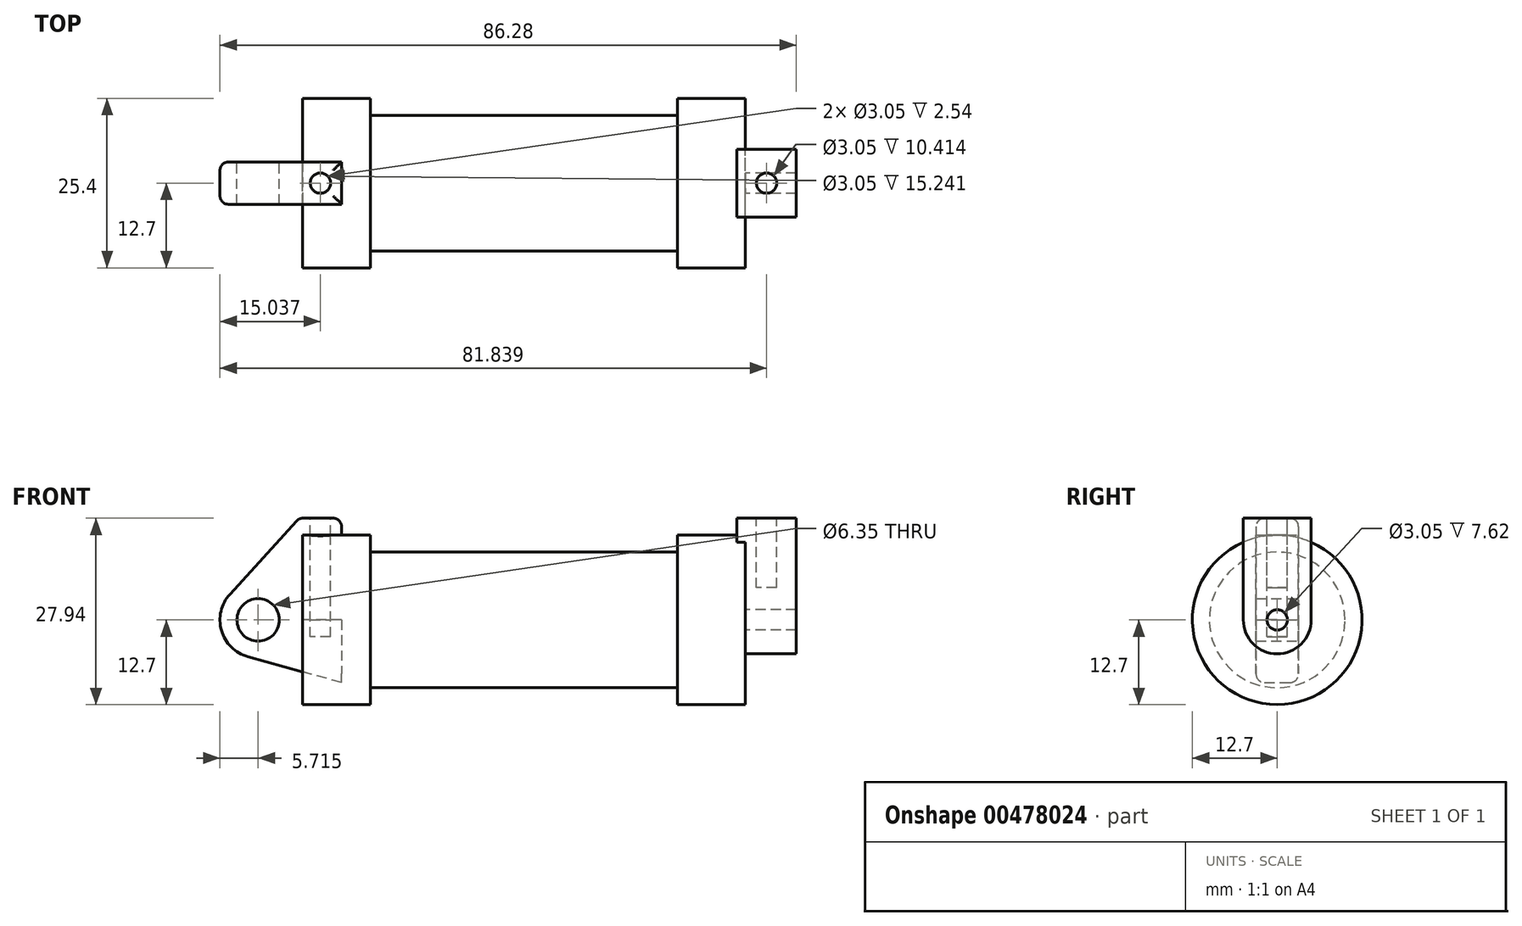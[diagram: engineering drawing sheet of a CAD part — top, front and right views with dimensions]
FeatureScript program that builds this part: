
annotation { "Feature Type Name" : "Feature", "Feature Type Description" : "" }
export const myFeature = defineFeature(function(context is Context, id is Id, definition is map)
    precondition{}
    {
        {
            var Q0;
            Q0=qCreatedBy(makeId("Front.planeOp"),FACE);
            var sketch = newSketch(context, id + "F0", { "sketchPlane" : qUnion([Q0])});
            skLineSegment(sketch, "E0", {"start": v(0, 0) * mm, "end": v(0, 12.7) * mm});
            skLineSegment(sketch, "E1", {"start": v(0, 12.7) * mm, "end": v(10.16, 12.7) * mm});
            skLineSegment(sketch, "E2", {"start": v(10.16, 12.7) * mm, "end": v(10.16, 10.16) * mm});
            skLineSegment(sketch, "E3", {"start": v(10.16, 10.16) * mm, "end": v(56.13, 10.16) * mm});
            skLineSegment(sketch, "E4", {"start": v(56.13, 10.16) * mm, "end": v(56.13, 12.7) * mm});
            skLineSegment(sketch, "E5", {"start": v(56.13, 12.7) * mm, "end": v(66.3, 12.7) * mm});
            skLineSegment(sketch, "E6", {"start": v(66.3, 12.7) * mm, "end": v(66.3, 0) * mm});
            skLineSegment(sketch, "E7", {"start": v(66.3, 0) * mm, "end": v(0, 0) * mm});
            skLineSegment(sketch, "E8", {"start": v(5.84, 15.24) * mm, "end": v(-0.5, 15.24) * mm});
            skLineSegment(sketch, "E9", {"start": v(-0.5, 15.24) * mm, "end": v(-10.88, 3.85) * mm});
            skLineSegment(sketch, "E10", {"start": v(0, 0) * mm, "end": v(-6.65, 0) * mm});
            skCircle(sketch, "E11", {"center": v(-6.65, 0) * mm, "radius": 5.72 * mm});
            skCircle(sketch, "E12", {"center": v(-6.65, 0) * mm, "radius": 3.18 * mm});
            skLineSegment(sketch, "E13", {"start": v(5.84, 15.24) * mm, "end": v(5.84, -9.4) * mm});
            skLineSegment(sketch, "E14", {"start": v(5.84, -9.4) * mm, "end": v(-8.18, -5.5) * mm});
            skSolve(sketch);
        }
        {
            var Q0;
            {var subQ0=sQuery(id+"F0.wireOp",EDGE,"E2");Q0=makeQuery(id+"F0.imprint","IMPRINT",FACE,{"disambiguationData":[TD([[makeQuery(id+"F0.imprint","IMPRINT",EDGE,{"derivedFrom":subQ0}),-1.0]])]});}
            var Q1;
            {var subQ0=sQuery(id+"F0.wireOp",EDGE,"E0");Q1=makeQuery(id+"F0.imprint","IMPRINT",FACE,{"disambiguationData":[TD([[makeQuery(id+"F0.imprint","IMPRINT",EDGE,{"derivedFrom":subQ0}),-1.0]])]});}
            var Q2;
            Q2=sQuery(id+"F0.wireOp",EDGE,"E7");
            revolve(context, id + "F1", {"entities" : qUnion([Q0, Q1]), "axis" : qUnion([Q2]), "revolveType" : RevolveType.FULL});
        }
        {
            var Q0;
            {var subQ5=sQuery(id+"F0.wireOp",EDGE,"E12");Q0=makeQuery(id+"F0.imprint","IMPRINT",FACE,{"disambiguationData":[TD([[makeQuery(id+"F0.imprint","IMPRINT",EDGE,{"derivedFrom":subQ5}),-1.0]])]});}
            var Q1;
            {var subQ0=sQuery(id+"F0.wireOp",EDGE,"E14");Q1=makeQuery(id+"F0.imprint","IMPRINT",FACE,{"disambiguationData":[TD([[makeQuery(id+"F0.imprint","IMPRINT",EDGE,{"derivedFrom":subQ0}),-1.0]])]});}
            var Q2;
            {var subQ1=sQuery(id+"F0.wireOp",EDGE,"E0");Q2=makeQuery(id+"F0.imprint","IMPRINT",FACE,{"disambiguationData":[TD([[makeQuery(id+"F0.imprint","IMPRINT",EDGE,{"derivedFrom":subQ1}),1.0]])]});}
            var Q3;
            Q3 = qSketchRegion(id + "F3", true);
            extrude(context, id + "F2", {"entities" : qUnion([Q0, Q1, Q2, Q3]), "endBound" : BoundingType.SYMMETRIC, "depth" : 6.35 * mm});
        }
        {
            var Q0;
            Q0=makeQuery(id+"F1.opRevolve","SWEPT_FACE",FACE,{"disambiguationData":[OSD([sQuery(id+"F0.wireOp",EDGE,"E6")])]});
            var sketch = newSketch(context, id + "F3", { "sketchPlane" : qUnion([Q0])});
            skCircle(sketch, "E15", {"center": v(0, 0) * mm, "radius": 1.52 * mm});
            skCircle(sketch, "E16", {"center": v(0, 0) * mm, "radius": 5.08 * mm});
            skLineSegment(sketch, "E17", {"start": v(-5.08, 0) * mm, "end": v(-5.08, 15.24) * mm});
            skLineSegment(sketch, "E18", {"start": v(5.08, 0) * mm, "end": v(5.08, 15.24) * mm});
            skLineSegment(sketch, "E19", {"start": v(-5.08, 15.24) * mm, "end": v(5.08, 15.24) * mm});
            skSolve(sketch);
        }
        {
            var Q0;
            {var subQ0=sQuery(id+"F3.wireOp",EDGE,"E19");Q0=makeQuery(id+"F3.imprint","IMPRINT",FACE,{"disambiguationData":[TD([[makeQuery(id+"F3.imprint","IMPRINT",EDGE,{"derivedFrom":subQ0}),-1.0]])]});}
            var Q1;
            {var subQ0=sQuery(id+"F3.wireOp",EDGE,"E17");var subQ1=sQuery(id+"F3.wireOp",EDGE,"E16");var subQ2=makeQuery(id+"F3.imprint","INTERSECT",VERTEX,{"derivedFrom":[subQ1,subQ0]});Q1=makeQuery(id+"F3.imprint","IMPRINT",FACE,{"disambiguationData":[TD([[makeQuery(id+"F3.imprint","IMPRINT",EDGE,{"disambiguationData":[TD([[subQ2,1.0]])],"derivedFrom":subQ1}),-1.0]])]});}
            var Q2;
            Q2=makeQuery(id+"F3.imprint","IMPRINT",FACE,{"disambiguationData":[TD([[makeQuery(id+"F3.imprint","IMPRINT",EDGE,{"derivedFrom":sQuery(id+"F3.wireOp",EDGE,"E15")}),-1.0]])]});
            extrude(context, id + "F4", {"entities" : qUnion([Q0, Q1, Q2]), "operationType" : NewBodyOperationType.ADD, "depth" : 7.62 * mm});
        }
        {
            var Q0;
            Q0=makeQuery(id+"F4.opExtrude","CAP_FACE",FACE,{"disambiguationData":[OSD([sQuery(id+"F3.wireOp",EDGE,"E15"),sQuery(id+"F3.wireOp",EDGE,"E16"),sQuery(id+"F3.wireOp",EDGE,"E17"),sQuery(id+"F3.wireOp",EDGE,"E18"),sQuery(id+"F3.wireOp",EDGE,"E19")])],"isStart":true});
            var Q1;
            Q1=makeQuery(id+"F4.boolean.opBoolean","SPLIT",FACE,{"disambiguationData":[TD([makeQuery(id+"F4.opExtrude","SWEPT_FACE",FACE,{"disambiguationData":[OSD([sQuery(id+"F3.wireOp",EDGE,"E15")])]})])],"derivedFrom":makeQuery(id+"F1.opRevolve","SWEPT_FACE",FACE,{"disambiguationData":[OSD([sQuery(id+"F0.wireOp",EDGE,"E6")])]})});
            extrude(context, id + "F5", {"entities" : qUnion([Q0, Q1]), "operationType" : NewBodyOperationType.ADD, "depth" : 1.27 * mm});
        }
        {
            var Q0;
            {var subQ0=sQuery(id+"F3.wireOp",EDGE,"E19");Q0=makeQuery(id+"F5.boolean.opBoolean","MERGE",FACE,{"derivedFrom":[makeQuery(id+"F4.opExtrude","SWEPT_FACE",FACE,{"disambiguationData":[OSD([subQ0])]}),makeQuery(id+"F5.opExtrude","SWEPT_FACE",FACE,{"disambiguationData":[OSD([subQ0])]})]});}
            var sketch = newSketch(context, id + "F6", { "sketchPlane" : qUnion([Q0])});
            skCircle(sketch, "E20", {"center": v(69.47, 0) * mm, "radius": 1.52 * mm});
            skLineSegment(sketch, "E21", {"start": v(69.47, 5.08) * mm, "end": v(69.47, -5.08) * mm, "construction": true});
            skSolve(sketch);
        }
        {
            var Q0;
            Q0=makeQuery(id+"F6.imprint","IMPRINT",FACE,{"disambiguationData":[TD([[makeQuery(id+"F6.imprint","IMPRINT",EDGE,{"derivedFrom":sQuery(id+"F6.wireOp",EDGE,"E20")}),1.0]])]});
            var Q1;
            Q1=sQuery(id+"F6.wireOp",EDGE,"E20");
            extrude(context, id + "F7", {"entities" : qUnion([Q0]), "operationType" : NewBodyOperationType.REMOVE, "surfaceEntities" : qUnion([Q1]), "oppositeDirection" : true, "depth" : 10.4 * mm});
        }
        {
            var Q0;
            Q0=makeQuery(id+"F2.opExtrude","SWEPT_FACE",FACE,{"disambiguationData":[OSD([sQuery(id+"F0.wireOp",EDGE,"E8")])]});
            var sketch = newSketch(context, id + "F8", { "sketchPlane" : qUnion([Q0])});
            skLineSegment(sketch, "E22", {"start": v(2.67, 3.18) * mm, "end": v(2.67, -3.18) * mm, "construction": true});
            skCircle(sketch, "E23", {"center": v(2.67, 0) * mm, "radius": 1.52 * mm});
            skSolve(sketch);
        }
        {
            var Q0;
            Q0=makeQuery(id+"F8.imprint","IMPRINT",FACE,{"disambiguationData":[TD([[makeQuery(id+"F8.imprint","IMPRINT",EDGE,{"derivedFrom":sQuery(id+"F8.wireOp",EDGE,"E23")}),1.0]])]});
            var Q1;
            Q1=sQuery(id+"F8.wireOp",EDGE,"E23");
            extrude(context, id + "F9", {"entities" : qUnion([Q0]), "operationType" : NewBodyOperationType.REMOVE, "surfaceEntities" : qUnion([Q1]), "oppositeDirection" : true, "depth" : 17.78 * mm});
        }
        {
            var Q0;
            {var subQ0=sQuery(id+"F3.wireOp",EDGE,"E17");var subQ1=sQuery(id+"F3.wireOp",EDGE,"E16");var subQ2=makeQuery(id+"F3.imprint","INTERSECT",VERTEX,{"derivedFrom":[subQ1,subQ0]});Q0=makeQuery(id+"F3.imprint","IMPRINT",FACE,{"disambiguationData":[TD([[makeQuery(id+"F3.imprint","IMPRINT",EDGE,{"disambiguationData":[TD([[subQ2,1.0]])],"derivedFrom":subQ1}),-1.0]])]});}
            extrude(context, id + "F10", {"entities" : qUnion([Q0]), "operationType" : NewBodyOperationType.ADD, "oppositeDirection" : true, "depth" : 1.27 * mm});
        }
        {
            var Q0;
            {var subQ0=sQuery(id+"F0.wireOp",EDGE,"E5");var subQ1=sQuery(id+"F0.wireOp",EDGE,"E6");Q0=makeQuery(id+"F4.boolean.opBoolean","SPLIT",EDGE,{"disambiguationData":[topologyDisambiguationEdgeConnected([makeQuery(id+"F1.opRevolve","SWEPT_FACE",FACE,{"disambiguationData":[OSD([subQ1])]})])],"derivedFrom":makeQuery(id+"F1.opRevolve","SWEPT_EDGE",EDGE,{"disambiguationData":[OSD([subQ0,subQ1])]})});}
            var Q1;
            {var subQ0=sQuery(id+"F3.wireOp",EDGE,"E17");Q1=makeQuery(id+"F4.boolean.opBoolean","SPLIT",EDGE,{"disambiguationData":[topologyDisambiguationEdgeConnected([makeQuery(id+"F1.opRevolve","SWEPT_FACE",FACE,{"disambiguationData":[OSD([sQuery(id+"F0.wireOp",EDGE,"E6")])]})])],"derivedFrom":makeQuery(id+"F4.opExtrude","CAP_EDGE",EDGE,{"disambiguationData":[OSD([subQ0])],"isStart":true})});}
            var Q2;
            Q2=makeQuery(id+"F4.opExtrude","CAP_EDGE",EDGE,{"disambiguationData":[OSD([sQuery(id+"F3.wireOp",EDGE,"E17")])],"isStart":false});
            var Q3;
            Q3=makeQuery(id+"F4.opExtrude","CAP_EDGE",EDGE,{"disambiguationData":[OSD([sQuery(id+"F3.wireOp",EDGE,"E19")])],"isStart":false});
            var Q4;
            {var subQ0=sQuery(id+"F3.wireOp",EDGE,"E19");var subQ1=sQuery(id+"F3.wireOp",EDGE,"E18");Q4=makeQuery(id+"F5.boolean.opBoolean","MERGE",EDGE,{"derivedFrom":[makeQuery(id+"F4.opExtrude","SWEPT_EDGE",EDGE,{"disambiguationData":[OSD([subQ1,subQ0])]}),makeQuery(id+"F5.opExtrude","SWEPT_EDGE",EDGE,{"disambiguationData":[OSD([subQ1,subQ0])]})]});}
            var Q5;
            Q5=makeQuery(id+"F5.opExtrude","CAP_EDGE",EDGE,{"disambiguationData":[OSD([sQuery(id+"F3.wireOp",EDGE,"E19")])],"isStart":false});
            var Q6;
            {var subQ0=sQuery(id+"F3.wireOp",EDGE,"E19");var subQ1=sQuery(id+"F3.wireOp",EDGE,"E17");Q6=makeQuery(id+"F5.boolean.opBoolean","MERGE",EDGE,{"derivedFrom":[makeQuery(id+"F4.opExtrude","SWEPT_EDGE",EDGE,{"disambiguationData":[OSD([subQ1,subQ0])]}),makeQuery(id+"F5.opExtrude","SWEPT_EDGE",EDGE,{"disambiguationData":[OSD([subQ1,subQ0])]})]});}
            var Q7;
            Q7=makeQuery(id+"F1.opRevolve","SWEPT_FACE",FACE,{"disambiguationData":[OSD([sQuery(id+"F0.wireOp",EDGE,"E4")])]});
            var Q8;
            Q8=makeQuery(id+"F1.opRevolve","SWEPT_EDGE",EDGE,{"disambiguationData":[OSD([sQuery(id+"F0.wireOp",EDGE,"E1"),sQuery(id+"F0.wireOp",EDGE,"E2")])]});
            var Q9;
            Q9=makeQuery(id+"F1.opRevolve","SWEPT_EDGE",EDGE,{"disambiguationData":[OSD([sQuery(id+"F0.wireOp",EDGE,"E2"),sQuery(id+"F0.wireOp",EDGE,"E3")])]});
            var Q10;
            Q10=makeQuery(id+"F2.opExtrude","CAP_EDGE",EDGE,{"disambiguationData":[OSD([sQuery(id+"F0.wireOp",EDGE,"E9")])],"isStart":false});
            var Q11;
            Q11=makeQuery(id+"F2.opExtrude","CAP_EDGE",EDGE,{"disambiguationData":[OSD([sQuery(id+"F0.wireOp",EDGE,"E8")])],"isStart":false});
            var Q12;
            Q12=makeQuery(id+"F1.opRevolve","SWEPT_EDGE",EDGE,{"disambiguationData":[OSD([sQuery(id+"F0.wireOp",EDGE,"E0"),sQuery(id+"F0.wireOp",EDGE,"E1")])]});
            var Q13;
            Q13=makeQuery(id+"F2.opExtrude","CAP_EDGE",EDGE,{"disambiguationData":[OSD([sQuery(id+"F0.wireOp",EDGE,"E9")])],"isStart":true});
            var Q14;
            Q14=makeQuery(id+"F2.opExtrude","CAP_EDGE",EDGE,{"disambiguationData":[OSD([sQuery(id+"F0.wireOp",EDGE,"E8")])],"isStart":true});
            var Q15;
            Q15=makeQuery(id+"F2.opExtrude","SWEPT_EDGE",EDGE,{"disambiguationData":[OSD([sQuery(id+"F0.wireOp",EDGE,"E8"),sQuery(id+"F0.wireOp",EDGE,"E9")])]});
            var Q16;
            Q16=makeQuery(id+"F2.opExtrude","SWEPT_EDGE",EDGE,{"disambiguationData":[OSD([sQuery(id+"F0.wireOp",EDGE,"E8"),sQuery(id+"F0.wireOp",EDGE,"E13")])]});
            fillet(context, id + "F11", {"entities" : qUnion([Q0, Q1, Q2, Q3, Q4, Q5, Q6, Q7, Q8, Q9, Q10, Q11, Q12, Q13, Q14, Q15, Q16]), "radius" : 1.27 * mm, "tangentPropagation" : true, "allowEdgeOverflow" : false});
        }
    });
